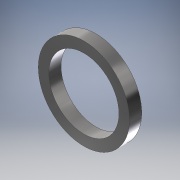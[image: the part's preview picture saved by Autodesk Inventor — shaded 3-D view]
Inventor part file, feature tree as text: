
AUTODESK INVENTOR PART (.ipt)
format: ipt  version: 2018 (Build 220112000, 112)  size: 104,960 bytes
history: native  units: mm
features: extrude x1, sketch x1
ambient origin geometry x8: Origin, YZ Plane, XZ Plane, XY Plane, X Axis, Y Axis, Z Axis, Center Point
bodies: Solid1 (feature_tree)
feature tree (2):
  extrude  "Extrusion1"  Depth=7.0mm
  sketch  "Sketch1"  dims[d0=40.0mm d1=52.0mm d2=7.0mm d3=0.0mm]
